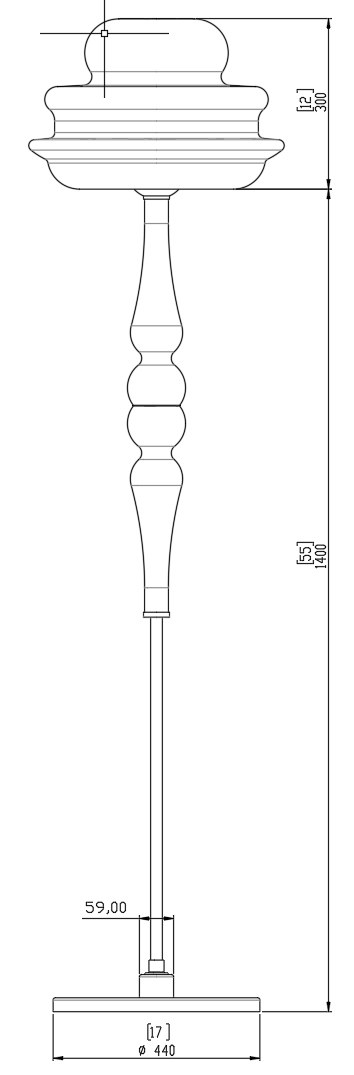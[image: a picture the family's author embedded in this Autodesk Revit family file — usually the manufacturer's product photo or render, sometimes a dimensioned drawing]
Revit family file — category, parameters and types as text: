
# Revit family: NARANZA-Suspension
name_source: partatom
category: Lighting Fixtures
units: mm (PartAtom-declared; Revit-internal decimal feet)

## family parameters
Always vertical = Yes
Cut with Voids When Loaded = No
Host = Ceiling
Light Source = No
OmniClass Number = 23.80.70.11
OmniClass Title = Luminaries for Internal Lighting
Part Type = Normal
Room Calculation Point = No
Round Connector Dimension = Use Diameter
Shared = No

## types (2) — shared parameters
Country = Europe
Description = SUSPENSION
Designer = Studio Debonademeo
Diameter Bulb = 15 mm  [stored 0.0492126 ft]
Manufacturer = Vistosi
Manufacturer country = Italy
Model = NARANZA
Type Comments = Studio Debonademeo
URL = https://vistosi.com
URL Product Page = https://vistosi.it
zero-valued in all types: Default Elevation, Depth

## per-type parameters (varying)
| type | Base_Type | Lampshade_Type | SP G | SP P | Width |
| NARANZA SP P | NARANZA_Base : NARANZA SP P | NARANZA_Lampshade : NARANZA SP P | No | Yes | 40 mm  [stored 0.131234 ft] |
| NARANZA SP G | NARANZA_Base : NARANZA SP G | NARANZA_Lampshade : NARANZA SP G | Yes | No | 57 mm  [stored 0.187008 ft] |

note: [stored X ft] marks values corroborated as IEEE doubles in the binary element streams (Revit-internal decimal feet)

## geometry (parser evidence)
native form markers: Sweep x12
no freeform markers — native parametric forms only
